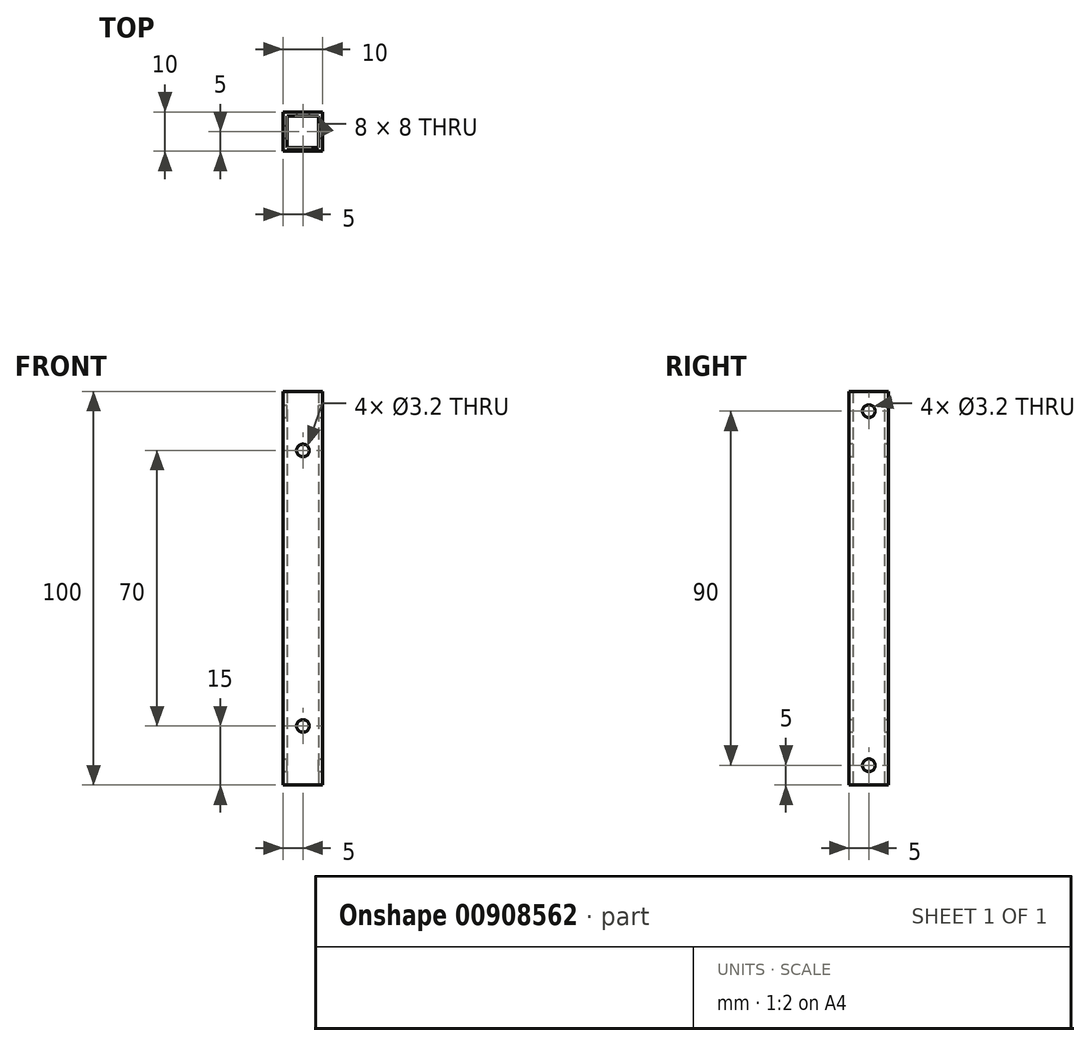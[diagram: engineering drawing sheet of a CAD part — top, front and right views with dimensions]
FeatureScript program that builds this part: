
annotation { "Feature Type Name" : "Feature", "Feature Type Description" : "" }
export const myFeature = defineFeature(function(context is Context, id is Id, definition is map)
    precondition{}
    {
        {
            var Q0;
            Q0=qCreatedBy(makeId("Top.planeOp"),FACE);
            var sketch = newSketch(context, id + "F0", { "sketchPlane" : qUnion([Q0])});
            skLineSegment(sketch, "E0.bottom", {"start": v(0, 0) * mm, "end": v(10, 0) * mm});
            skLineSegment(sketch, "E0.top", {"start": v(0, -10) * mm, "end": v(10, -10) * mm});
            skLineSegment(sketch, "E0.left", {"start": v(0, 0) * mm, "end": v(0, -10) * mm});
            skLineSegment(sketch, "E0.right", {"start": v(10, 0) * mm, "end": v(10, -10) * mm});
            skLineSegment(sketch, "E1.bottom", {"start": v(1, -1) * mm, "end": v(9, -1) * mm});
            skLineSegment(sketch, "E1.top", {"start": v(1, -9) * mm, "end": v(9, -9) * mm});
            skLineSegment(sketch, "E1.left", {"start": v(1, -1) * mm, "end": v(1, -9) * mm});
            skLineSegment(sketch, "E1.right", {"start": v(9, -1) * mm, "end": v(9, -9) * mm});
            skSolve(sketch);
        }
        {
            var Q0;
            Q0 = qSketchRegion(id + "F0", true);
            extrude(context, id + "F1", {"entities" : qUnion([Q0]), "depth" : 100 * mm, "offsetDistance" : 25 * mm});
        }
        {
            var Q0;
            Q0=makeQuery(id+"F1.opExtrude","SWEPT_FACE",FACE,{"disambiguationData":[OSD([sQuery(id+"F0.wireOp",EDGE,"E0.right")])]});
            var sketch = newSketch(context, id + "F2", { "sketchPlane" : qUnion([Q0])});
            skCircle(sketch, "E2", {"center": v(-5, 5) * mm, "radius": 1.6 * mm});
            skPoint(sketch, "E3", {"position": v(-5, 95) * mm});
            skSolve(sketch);
        }
        {
            var Q0;
            Q0=makeQuery(id+"F2.imprint","IMPRINT",FACE,{"disambiguationData":[TD([[makeQuery(id+"F2.imprint","IMPRINT",EDGE,{"derivedFrom":sQuery(id+"F2.wireOp",EDGE,"E2")}),1.0]])]});
            extrude(context, id + "F3", {"entities" : qUnion([Q0]), "operationType" : NewBodyOperationType.REMOVE, "oppositeDirection" : true, "depth" : 25 * mm, "offsetDistance" : 25 * mm});
        }
        {
            var Q0;
            Q0=sQuery(id+"F2.wireOp",VERTEX,"E3");
            var Q1;
            Q1=makeQuery(id+"F1.opExtrude","SWEPT_BODY",BODY,{"disambiguationData":[OSD([sQuery(id+"F0.wireOp",EDGE,"E0.bottom"),sQuery(id+"F0.wireOp",EDGE,"E0.top"),sQuery(id+"F0.wireOp",EDGE,"E0.left"),sQuery(id+"F0.wireOp",EDGE,"E0.right"),sQuery(id+"F0.wireOp",EDGE,"E1.bottom"),sQuery(id+"F0.wireOp",EDGE,"E1.top"),sQuery(id+"F0.wireOp",EDGE,"E1.left"),sQuery(id+"F0.wireOp",EDGE,"E1.right")])]});
            hole(context, id + "F4", {"style" : HoleStyle.SIMPLE, "endStyle" : HoleEndStyle.THROUGH, "holeDiameter" : 3.2 * mm, "majorDiameter" : 5 * mm, "isTappedThrough" : true, "tappedDepth" : 12 * mm, "tapClearance" : 3, "locations" : qUnion([Q0]), "scope" : qUnion([Q1])});
        }
        {
            var Q0;
            Q0=makeQuery(id+"F1.opExtrude","SWEPT_FACE",FACE,{"disambiguationData":[OSD([sQuery(id+"F0.wireOp",EDGE,"E0.top")])]});
            var sketch = newSketch(context, id + "F5", { "sketchPlane" : qUnion([Q0])});
            skPoint(sketch, "E4", {"position": v(5, 15) * mm});
            skPoint(sketch, "E5", {"position": v(5, 85) * mm});
            skSolve(sketch);
        }
        {
            var Q0;
            Q0=sQuery(id+"F5.wireOp",VERTEX,"E4");
            var Q1;
            Q1=sQuery(id+"F5.wireOp",VERTEX,"E5");
            var Q2;
            Q2=makeQuery(id+"F1.opExtrude","SWEPT_BODY",BODY,{"disambiguationData":[OSD([sQuery(id+"F0.wireOp",EDGE,"E0.bottom"),sQuery(id+"F0.wireOp",EDGE,"E0.top"),sQuery(id+"F0.wireOp",EDGE,"E0.left"),sQuery(id+"F0.wireOp",EDGE,"E0.right"),sQuery(id+"F0.wireOp",EDGE,"E1.bottom"),sQuery(id+"F0.wireOp",EDGE,"E1.top"),sQuery(id+"F0.wireOp",EDGE,"E1.left"),sQuery(id+"F0.wireOp",EDGE,"E1.right")])]});
            hole(context, id + "F6", {"style" : HoleStyle.SIMPLE, "endStyle" : HoleEndStyle.THROUGH, "holeDiameter" : 3.2 * mm, "majorDiameter" : 5 * mm, "isTappedThrough" : true, "tappedDepth" : 12 * mm, "tapClearance" : 3, "locations" : qUnion([Q0, Q1]), "scope" : qUnion([Q2])});
        }
    });
